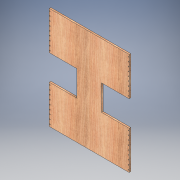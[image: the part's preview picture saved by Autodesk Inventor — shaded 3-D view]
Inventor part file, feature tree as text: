
AUTODESK INVENTOR PART (.ipt)
format: ipt  version: 2018 (Build 220112000, 112)  size: 197,120 bytes
history: native  units: in
note: dims shown in document units (in); Inventor stores cm internally (conversion verified against a paired STEP export)
features: extrude x2, sketch x2
ambient origin geometry x8: Origin, YZ Plane, XZ Plane, XY Plane, X Axis, Y Axis, Z Axis, Center Point
bodies: Solid1 (feature_tree)
feature tree (4):
  extrude  "Extrusion1"  Depth=9.0in
  extrude  "Extrusion2"  Depth=6.0in
  sketch  "Sketch1"  dims[d0=18.75in d1=9.0in]
  sketch  "Sketch2"  dims[d2=6.5in d3=6.0in d4=9.0in d5=6.5in d6=0.375in d7=0.0in d8=0.125in d9=0.5in d10=1.0in d11=1.0in d12=1.0in d13=1.0in d14=1.0in d15=1.0in d16=1.0in d17=1.0in d18=0.2031in d19=3.25in d20=0.0in]
